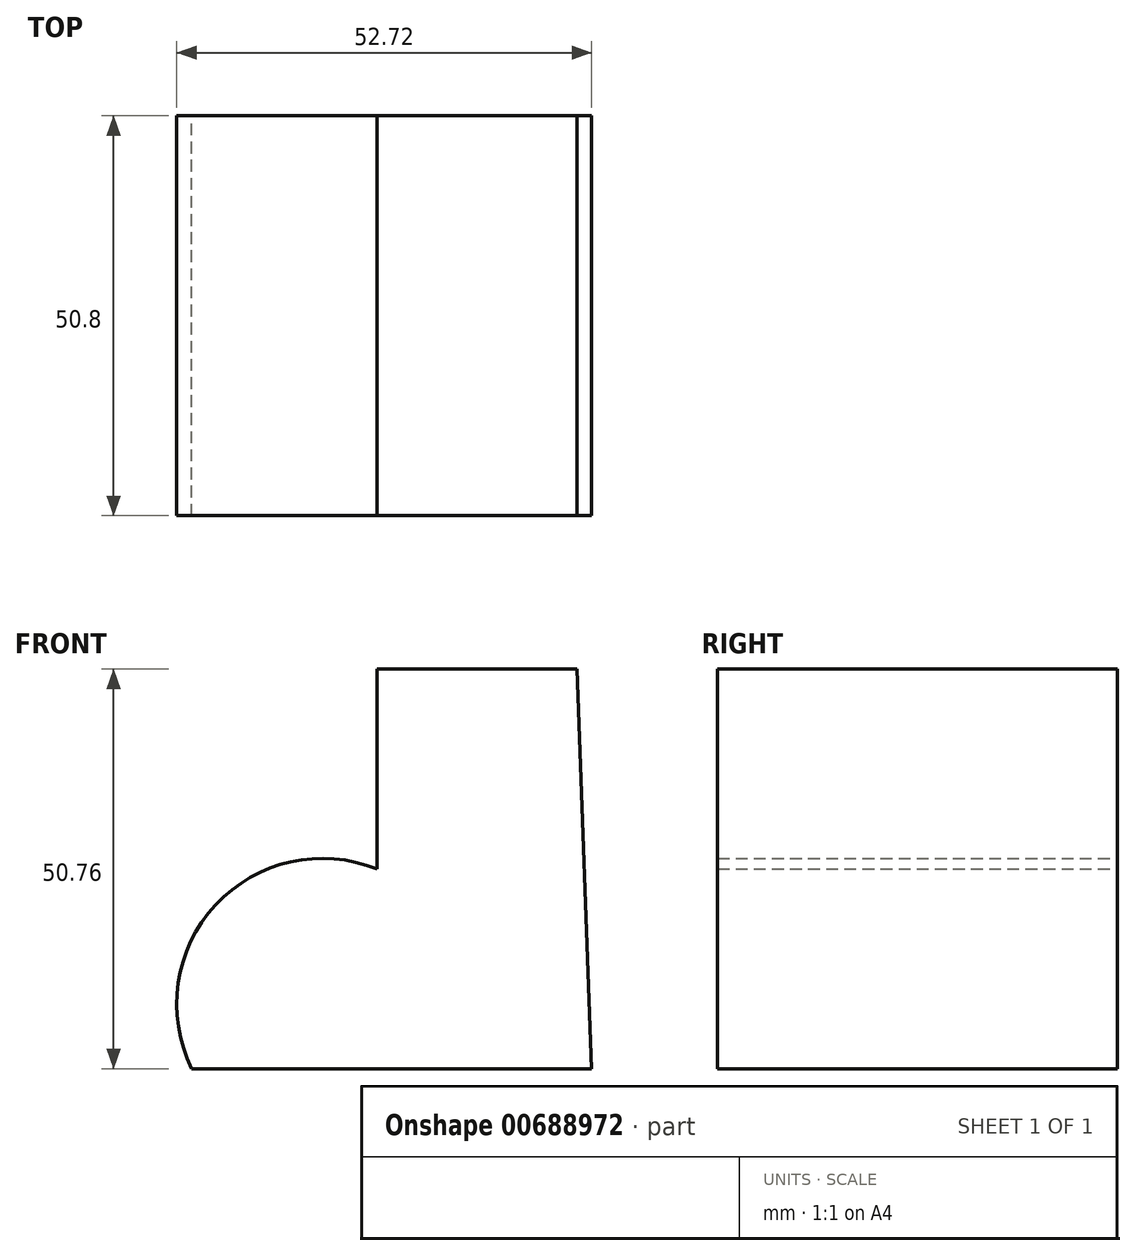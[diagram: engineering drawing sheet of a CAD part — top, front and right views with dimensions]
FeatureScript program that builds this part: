
annotation { "Feature Type Name" : "Feature", "Feature Type Description" : "" }
export const myFeature = defineFeature(function(context is Context, id is Id, definition is map)
    precondition{}
    {
        {
            var Q0;
            Q0=qCreatedBy(makeId("Front.planeOp"),FACE);
            var sketch = newSketch(context, id + "F0", { "sketchPlane" : qUnion([Q0])});
            skLineSegment(sketch, "E0", {"start": v(20.98, 41.53) * mm, "end": v(22.83, -9.23) * mm});
            skLineSegment(sketch, "E1", {"start": v(22.83, -9.23) * mm, "end": v(-27.97, -9.23) * mm});
            skLineSegment(sketch, "E2", {"start": v(20.98, 41.53) * mm, "end": v(-4.42, 41.53) * mm});
            skLineSegment(sketch, "E3", {"start": v(-4.42, 41.53) * mm, "end": v(-4.42, 16.13) * mm});
            skArc(sketch, "E4", {"start": v(-4.42, 16.13) * mm, "mid": v(-24.94, 11.57) * mm, "end": v(-27.97, -9.23) * mm});
            skSolve(sketch);
        }
        {
            var Q0;
            Q0 = qSketchRegion(id + "F0", true);
            extrude(context, id + "F1", {"entities" : qUnion([Q0]), "depth" : 50.8 * mm, "offsetDistance" : 25.4 * mm});
        }
    });
